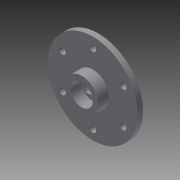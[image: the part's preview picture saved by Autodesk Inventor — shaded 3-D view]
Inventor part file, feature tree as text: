
AUTODESK INVENTOR PART (.ipt)
format: ipt  version: 2014 (Build 180170000, 170)  size: 129,536 bytes
history: native  units: mm
features: extrude x2, sketch x2
ambient origin geometry x8: Origin, YZ Plane, XZ Plane, XY Plane, X Axis, Y Axis, Z Axis, Center Point
bodies: Body1 (feature_tree)
feature tree (4):
  extrude  "Extrusion3"  Depth=17.2mm
  extrude  "Extrusion4"  TaperAngle=60.0deg  [1 undecoded]
  sketch  "Sketch1"  dims[d0=82.0mm d1=17.2mm]
  sketch  "Sketch2"  dims[d6=6.1mm d8=60.0deg d11=60.0deg d23=17.2mm d29=17.2mm d32=12.0mm d34=17.2mm d35=60.0deg d36=32.0mm d37=32.0mm d38=60.0deg d39=60.0deg d40=60.0deg d41=60.0deg d43=32.0mm d44=32.0mm d45=32.0mm d46=32.0mm d47=60.0deg d48=5.0mm d49=0.0mm d50=6.1mm d51=6.1mm d52=6.1mm d53=6.1mm d54=6.1mm d55=20.0mm d56=30.0mm d57=10.0mm d58=0.0mm]
note: 1 required parameter value undecoded (feature->parameter linkage not recoverable at this tier; creation-order binding heuristic only, values carry confidence <= 0.55)
